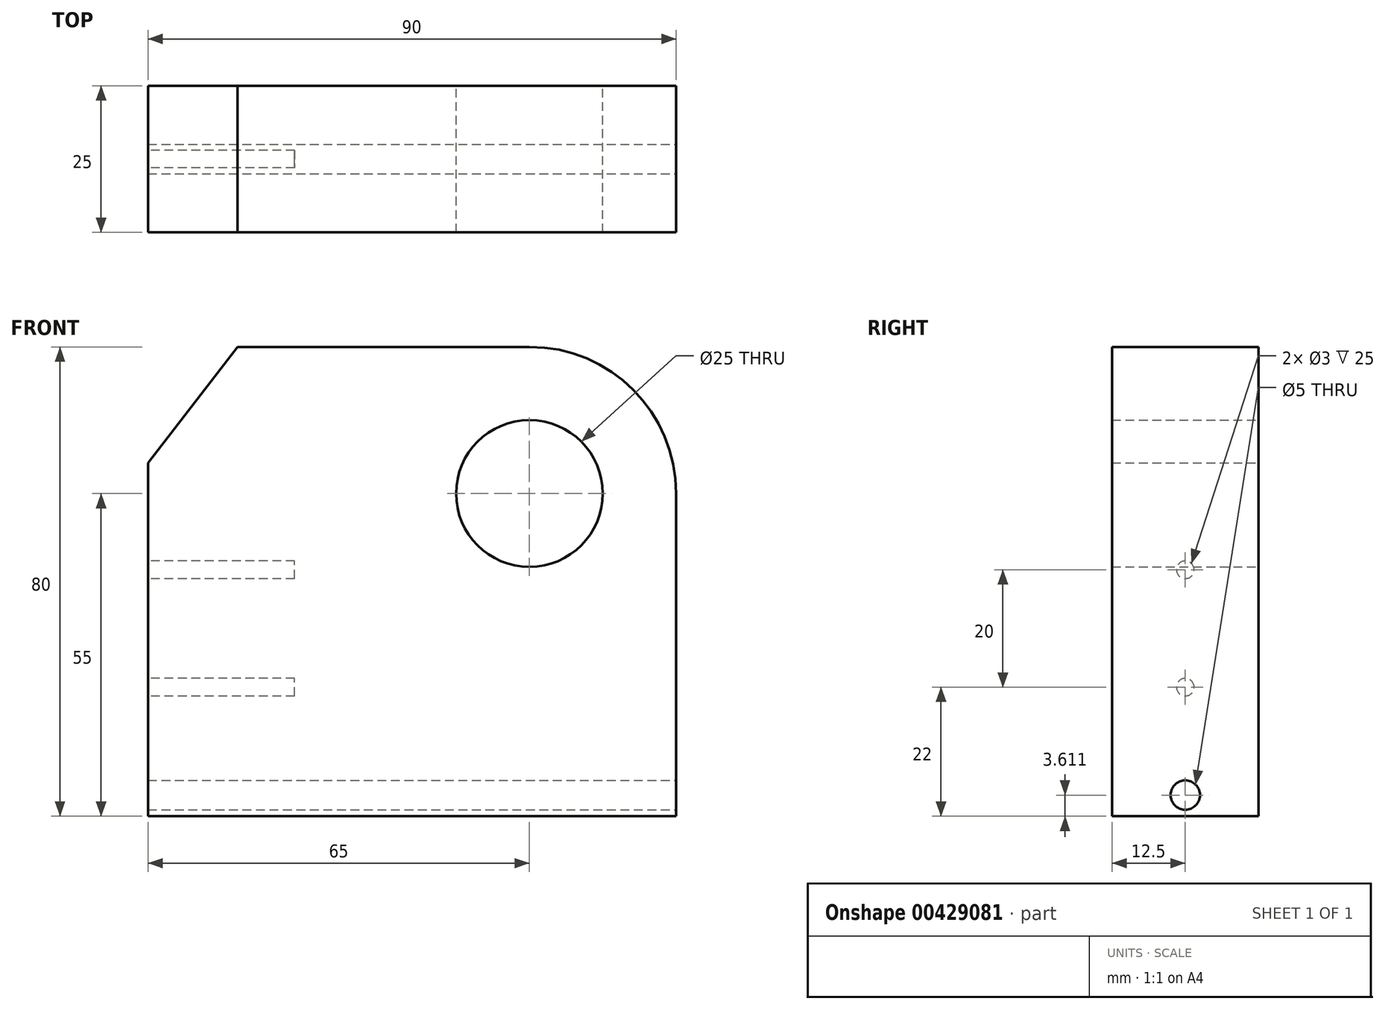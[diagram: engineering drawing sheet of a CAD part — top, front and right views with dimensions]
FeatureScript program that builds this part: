
annotation { "Feature Type Name" : "Feature", "Feature Type Description" : "" }
export const myFeature = defineFeature(function(context is Context, id is Id, definition is map)
    precondition{}
    {
        {
            var Q0;
            Q0=qCreatedBy(makeId("Front.planeOp"),FACE);
            var sketch = newSketch(context, id + "F0", { "sketchPlane" : qUnion([Q0])});
            skLineSegment(sketch, "E0.bottom", {"start": v(15.28, 80) * mm, "end": v(65, 80) * mm});
            skLineSegment(sketch, "E0.top", {"start": v(0, 0) * mm, "end": v(90, 0) * mm});
            skLineSegment(sketch, "E0.left", {"start": v(0, 60.21) * mm, "end": v(0, 0) * mm});
            skLineSegment(sketch, "E0.right", {"start": v(90, 55) * mm, "end": v(90, 0) * mm});
            skPoint(sketch, "E1.visualSharp", {"position": v(90, 80) * mm});
            skArc(sketch, "E1.filletArc", {"start": v(90, 55) * mm, "mid": v(82.68, 72.68) * mm, "end": v(65, 80) * mm});
            skCircle(sketch, "E2", {"center": v(65, 55) * mm, "radius": 12.5 * mm});
            skLineSegment(sketch, "E3", {"start": v(0, 60.21) * mm, "end": v(15.28, 80) * mm});
            skPoint(sketch, "E4.orphan", {"position": v(0, 80) * mm});
            skLineSegment(sketch, "E5", {"start": v(25.67, 80) * mm, "end": v(0, 40.05) * mm});
            skLineSegment(sketch, "E6", {"start": v(0, 60.21) * mm, "end": v(0, 40.05) * mm});
            skLineSegment(sketch, "E7", {"start": v(15.28, 80) * mm, "end": v(25.67, 80) * mm});
            skSolve(sketch);
        }
        {
            var Q0;
            Q0 = qSketchRegion(id + "F0", true);
            extrude(context, id + "F1", {"entities" : qUnion([Q0]), "endBound" : BoundingType.SYMMETRIC, "depth" : 25 * mm});
        }
        {
            var Q0;
            Q0 = qSketchRegion(id + "F0", true);
            extrude(context, id + "F2", {"entities" : qUnion([Q0]), "operationType" : NewBodyOperationType.REMOVE, "endBound" : BoundingType.THROUGH_ALL, "oppositeDirection" : true, "depth" : 25 * mm, "offsetDistance" : 25 * mm});
        }
        {
            var Q0;
            Q0 = qSketchRegion(id + "F0", true);
            var Q1;
            Q1 = qSketchRegion(id + "F4", true);
            extrude(context, id + "F3", {"entities" : qUnion([Q0, Q1]), "operationType" : NewBodyOperationType.ADD, "endBound" : BoundingType.SYMMETRIC, "depth" : 25 * mm, "offsetDistance" : 25 * mm});
        }
        {
            var Q0;
            Q0=qCreatedBy(makeId("Right.planeOp"),FACE);
            var sketch = newSketch(context, id + "F4", { "sketchPlane" : qUnion([Q0])});
            skCircle(sketch, "E8", {"center": v(0, 22) * mm, "radius": 1.5 * mm});
            skCircle(sketch, "E9", {"center": v(0, 42) * mm, "radius": 1.5 * mm});
            skCircle(sketch, "E10", {"center": v(0, 8) * mm, "radius": 2.5 * mm});
            skSolve(sketch);
        }
        {
            var Q0;
            Q0=makeQuery(id+"F4.imprint","IMPRINT",FACE,{"disambiguationData":[TD([[makeQuery(id+"F4.imprint","IMPRINT",EDGE,{"derivedFrom":sQuery(id+"F4.wireOp",EDGE,"E8")}),1.0]])]});
            var Q1;
            Q1=makeQuery(id+"F4.imprint","IMPRINT",FACE,{"disambiguationData":[TD([[makeQuery(id+"F4.imprint","IMPRINT",EDGE,{"derivedFrom":sQuery(id+"F4.wireOp",EDGE,"E9")}),1.0]])]});
            extrude(context, id + "F5", {"entities" : qUnion([Q0, Q1]), "operationType" : NewBodyOperationType.REMOVE, "depth" : 25 * mm, "offsetDistance" : 25 * mm});
        }
        {
            var Q0;
            {var subQ0=sQuery(id+"F0.wireOp",EDGE,"E0.right");Q0=makeQuery(id+"F3.boolean.opBoolean","MERGE",FACE,{"derivedFrom":[makeQuery(id+"F1.opExtrude","SWEPT_FACE",FACE,{"disambiguationData":[OSD([subQ0])]}),makeQuery(id+"F3.opExtrude","SWEPT_FACE",FACE,{"disambiguationData":[OSD([subQ0])]})]});}
            var sketch = newSketch(context, id + "F6", { "sketchPlane" : qUnion([Q0])});
            skCircle(sketch, "E11", {"center": v(0, 3.61) * mm, "radius": 2.5 * mm});
            skSolve(sketch);
        }
        {
            var Q0;
            Q0 = qSketchRegion(id + "F6", true);
            extrude(context, id + "F7", {"entities" : qUnion([Q0]), "operationType" : NewBodyOperationType.REMOVE, "endBound" : BoundingType.THROUGH_ALL, "oppositeDirection" : true, "depth" : 25 * mm, "offsetDistance" : 25 * mm});
        }
    });
